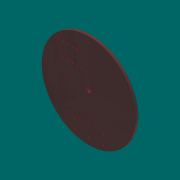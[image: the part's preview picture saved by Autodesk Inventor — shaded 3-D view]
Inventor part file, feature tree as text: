
AUTODESK INVENTOR PART (.ipt)
format: ipt  version: 2013 (Build 170138000, 138)  size: 138,240 bytes
history: native  units: mm
features: sketch x4, extrude x2, hole x2, other x1
ambient origin geometry x8: Origin, YZ Plane, XZ Plane, XY Plane, X Axis, Y Axis, Z Axis, Center Point
feature tree (9):
  other  "ソリッド1"
  extrude  "押し出し1"  Depth=200.0mm
  hole  "穴5"  [1 undecoded]
  extrude  "押し出し4"  Depth=8.0mm
  hole  "穴6"  [1 undecoded]
  sketch  "スケッチ1"
  sketch  "スケッチ12"
  sketch  "スケッチ13"
  sketch  "スケッチ14"
note: 2 required parameter values undecoded (feature->parameter linkage not recoverable at this tier; creation-order binding heuristic only, values carry confidence <= 0.55)
